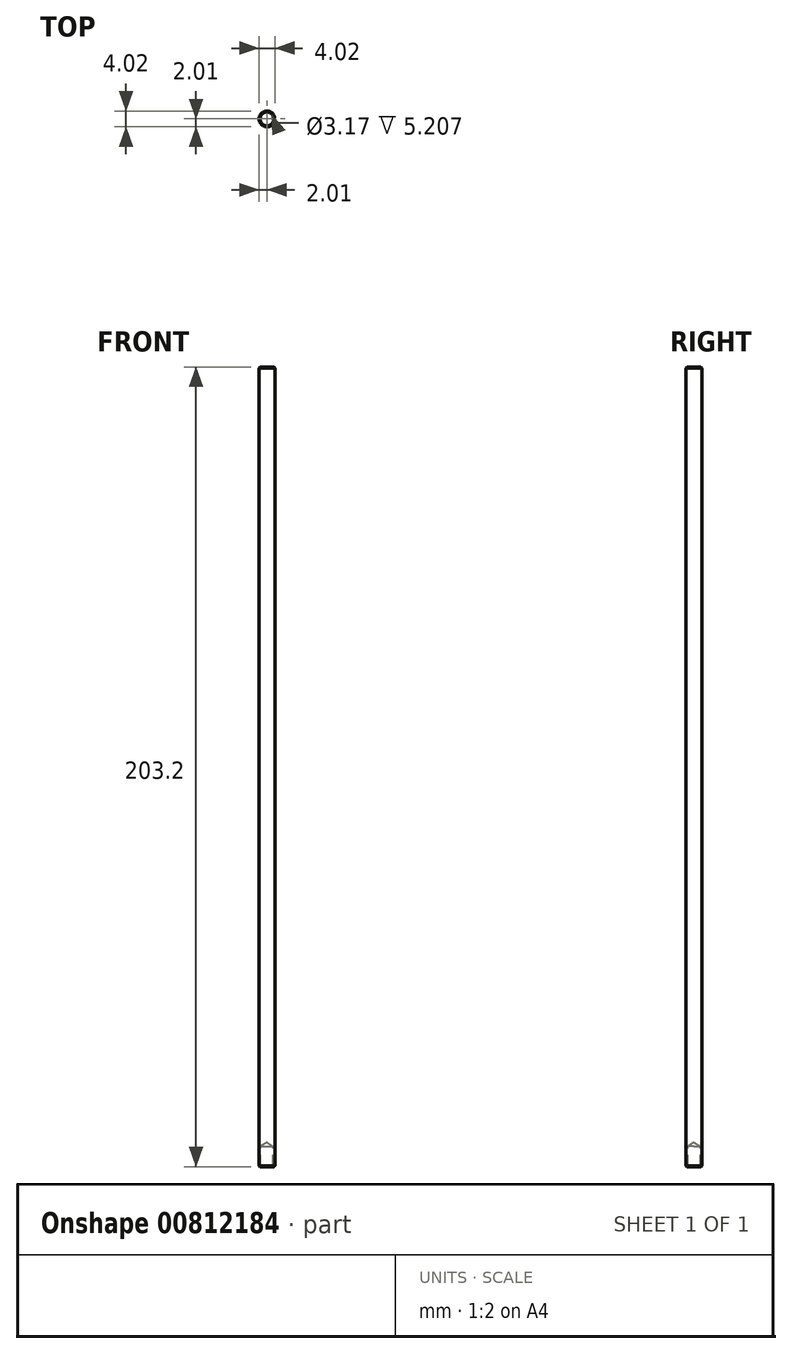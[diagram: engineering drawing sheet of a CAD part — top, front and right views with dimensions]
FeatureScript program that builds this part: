
annotation { "Feature Type Name" : "Feature", "Feature Type Description" : "" }
export const myFeature = defineFeature(function(context is Context, id is Id, definition is map)
    precondition{}
    {
        {
            var Q0;
            Q0=qCreatedBy(makeId("Top.planeOp"),FACE);
            var sketch = newSketch(context, id + "F0", { "sketchPlane" : qUnion([Q0])});
            skCircle(sketch, "E0", {"center": v(0, 0) * mm, "radius": 2 * mm});
            skSolve(sketch);
        }
        {
            var Q0;
            Q0=makeQuery(id+"F0.imprint","IMPRINT",FACE,{"disambiguationData":[TD([[makeQuery(id+"F0.imprint","IMPRINT",EDGE,{"derivedFrom":sQuery(id+"F0.wireOp",EDGE,"E0")}),1.0]])]});
            extrude(context, id + "F1", {"entities" : qUnion([Q0]), "depth" : 203.2 * mm, "offsetDistance" : 25.4 * mm});
        }
        {
            var Q0;
            Q0=makeQuery(id+"F1.opExtrude","CAP_EDGE",EDGE,{"disambiguationData":[OSD([sQuery(id+"F0.wireOp",EDGE,"E0")])],"isStart":true});
            var Q1;
            Q1=makeQuery(id+"F1.opExtrude","CAP_EDGE",EDGE,{"disambiguationData":[OSD([sQuery(id+"F0.wireOp",EDGE,"E0")])],"isStart":false});
            chamfer(context, id + "F2", {"entities" : qUnion([Q0, Q1]), "width" : 0.25 * mm, "tangentPropagation" : true});
        }
        {
            var Q0;
            Q0=sQuery(id+"F0.wireOp",VERTEX,"E0.center");
            var Q1;
            Q1=makeQuery(id+"F1.opExtrude","SWEPT_BODY",BODY,{"disambiguationData":[OSD([sQuery(id+"F0.wireOp",EDGE,"E0")])]});
            hole(context, id + "F3", {"style" : HoleStyle.SIMPLE, "endStyle" : HoleEndStyle.BLIND, "oppositeDirection" : true, "holeDiameter" : 3.17 * mm, "majorDiameter" : 6.35 * mm, "holeDepth" : 5.2 * mm, "isTappedThrough" : true, "tappedDepth" : 12.7 * mm, "tapClearance" : 3, "locations" : qUnion([Q0]), "scope" : qUnion([Q1]), "startStyle" : HoleStartStyle.SKETCH});
        }
    });
